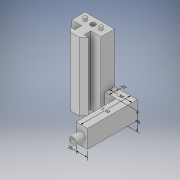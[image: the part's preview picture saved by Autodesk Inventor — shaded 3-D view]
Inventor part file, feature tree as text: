
AUTODESK INVENTOR PART (.ipt)
format: ipt  version: 2018 (Build 220112000, 112)  size: 195,584 bytes
history: native  units: in
note: dims shown in document units (in); Inventor stores cm internally (conversion verified against a paired STEP export)
features: sketch x9, extrude x7, other x6, hole x2
ambient origin geometry x8: Origin, YZ Plane, XZ Plane, XY Plane, X Axis, Y Axis, Z Axis, Center Point
bodies: Solid1 (feature_tree)
feature tree (24):
  other  "Annotations"
  extrude  "Extrusion1"  Depth=0.3in
  extrude  "Extrusion2"  Depth=0.25in
  extrude  "Extrusion3"  Depth=0.05in
  hole  "Hole1"  [1 undecoded]
  extrude  "Extrusion4"  Depth=0.1in
  sketch  "Sketch8"  dims[d10=1.5in d11=0.0in d12=0.15in]
  extrude  "Extrusion5"  Depth=0.15in
  extrude  "Extrusion6"  Depth=0.05in TaperAngle=0.0deg
  hole  "Hole2"  [1 undecoded]
  extrude  "Extrusion7"  Depth=0.5in
  sketch  "Sketch1"  dims[d0=0.65in d1=0.3in]
  sketch  "Sketch2"  dims[d2=0.1in d3=0.25in]
  sketch  "Sketch3"  dims[d4=0.2in d5=0.05in]
  sketch  "Sketch6"  dims[d6=0.1in d7=0.1in]
  sketch  "Sketch7"  dims[d8=0.1in d9=0.1in]
  sketch  "Sketch11"  dims[d14=0.08in d18=0.05in d19=0.0in]
  sketch  "Sketch12"  dims[d20=0.15in d21=0.08in]
  sketch  "Sketch13"  dims[d22=0.05in d23=0.0in d24=0.325in d25=0.11in d26=0.11in d27=0.75in d28=0.375in d29=0.25in d30=0.5635in d31=0.45in d32=0.8108in d33=0.215in d34=0.4in d35=0.5in d36=0.0in d39=0.885in d40=0.0in d41=0.125in d42=0.16in d43=0.2in d44=0.0in d45=0.11in d46=0.11in d47=0.75in d48=0.375in d49=0.25in d50=0.5635in d51=0.5in d52=0.8108in d68=0.05in d69=0.0in d53=0.2066in d54=0.0676in d55=0.4in d56=0.1242in d57=0.2866in d58=0.215in d59=0.228in d60=0.2946in d61=1.1in d62=0.1169in d63=0.3258in d64=0.25in d65=0.0498in d66=0.2036in d67=0.5in]
  other  "Linear Dimension 1"
  other  "Linear Dimension 2"
  other  "Linear Dimension 3"
  other  "Linear Dimension 4"
  other  "Linear Dimension 5"
note: 2 required parameter values undecoded (feature->parameter linkage not recoverable at this tier; creation-order binding heuristic only, values carry confidence <= 0.55)
